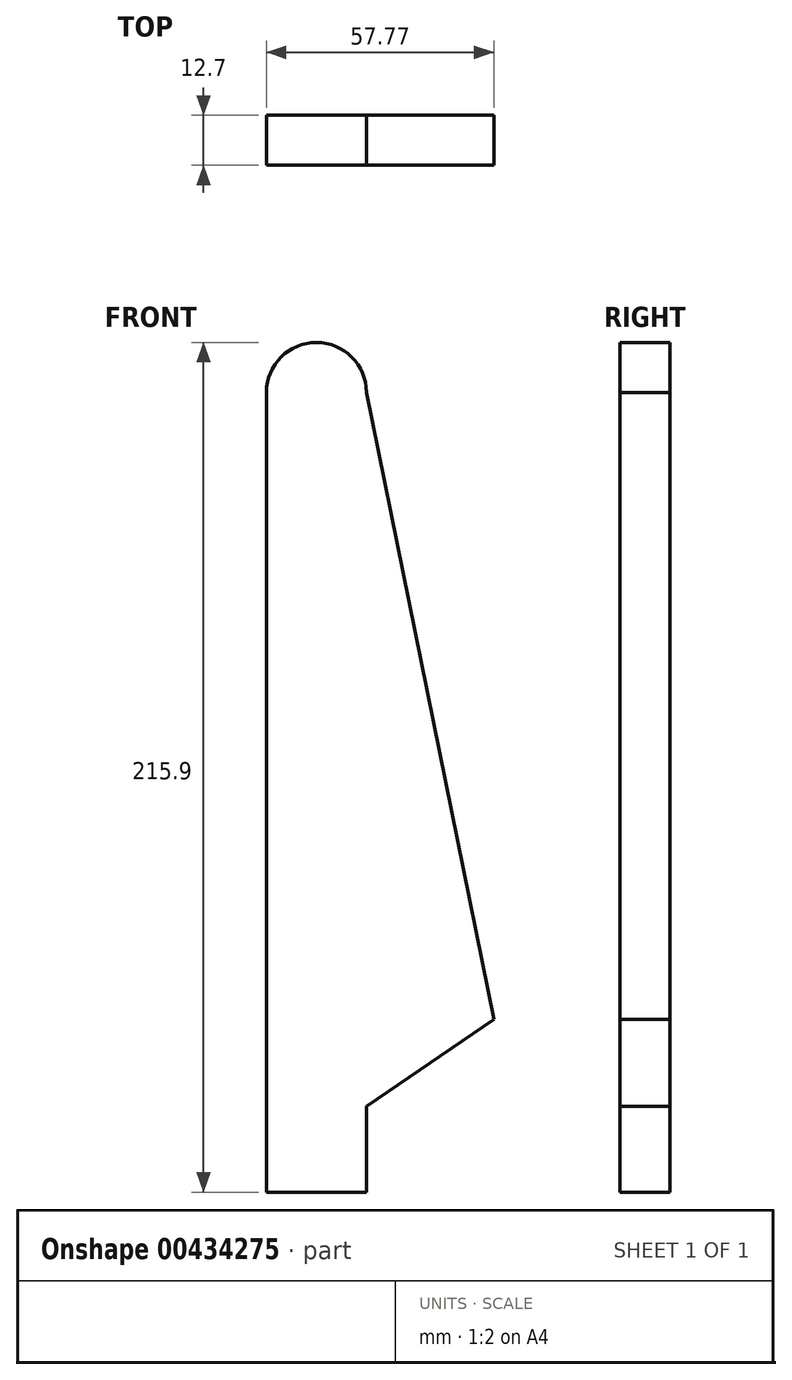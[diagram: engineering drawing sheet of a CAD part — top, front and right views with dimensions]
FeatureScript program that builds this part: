
annotation { "Feature Type Name" : "Feature", "Feature Type Description" : "" }
export const myFeature = defineFeature(function(context is Context, id is Id, definition is map)
    precondition{}
    {
        {
            var Q0;
            Q0=qCreatedBy(makeId("Front.planeOp"),FACE);
            var sketch = newSketch(context, id + "F0", { "sketchPlane" : qUnion([Q0])});
            skLineSegment(sketch, "E0", {"start": v(0, -98.82) * mm, "end": v(0, 104.38) * mm});
            skArc(sketch, "E1", {"start": v(25.4, 104.38) * mm, "mid": v(12.7, 117.08) * mm, "end": v(0, 104.38) * mm});
            skLineSegment(sketch, "E2", {"start": v(25.4, 104.38) * mm, "end": v(57.77, -54.92) * mm});
            skLineSegment(sketch, "E3", {"start": v(57.77, -54.92) * mm, "end": v(25.4, -77.02) * mm});
            skLineSegment(sketch, "E4", {"start": v(0, -98.82) * mm, "end": v(25.4, -98.82) * mm});
            skLineSegment(sketch, "E5", {"start": v(25.4, -98.82) * mm, "end": v(25.4, -77.02) * mm});
            skSolve(sketch);
        }
        {
            var Q0;
            Q0=makeQuery(id+"F0.imprint","IMPRINT",FACE,{"disambiguationData":[TD([[makeQuery(id+"F0.imprint","IMPRINT",EDGE,{"derivedFrom":sQuery(id+"F0.wireOp",EDGE,"E0")}),-1.0]])]});
            extrude(context, id + "F1", {"entities" : qUnion([Q0]), "depth" : 12.7 * mm});
        }
    });
